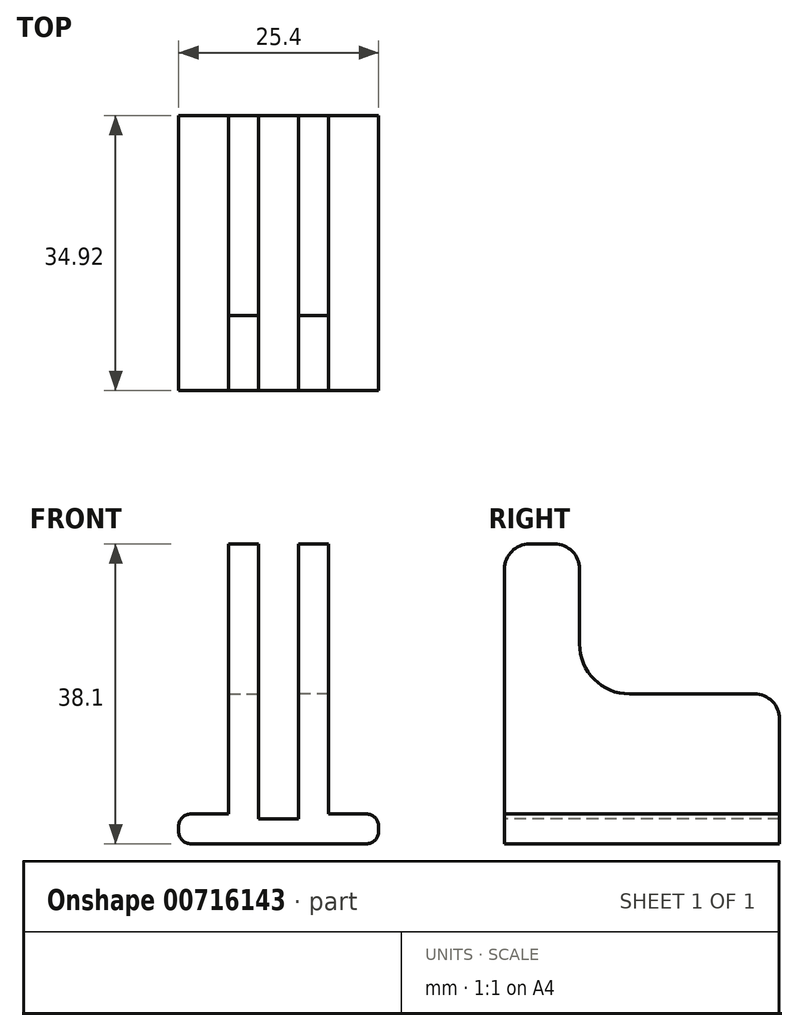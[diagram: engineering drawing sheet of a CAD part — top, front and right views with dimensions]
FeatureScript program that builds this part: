
annotation { "Feature Type Name" : "Feature", "Feature Type Description" : "" }
export const myFeature = defineFeature(function(context is Context, id is Id, definition is map)
    precondition{}
    {
        {
            var Q0;
            Q0=qCreatedBy(makeId("Right.planeOp"),FACE);
            var sketch = newSketch(context, id + "F0", { "sketchPlane" : qUnion([Q0])});
            skLineSegment(sketch, "E0", {"start": v(0, 0) * mm, "end": v(34.92, 0) * mm});
            skLineSegment(sketch, "E1", {"start": v(34.92, 0) * mm, "end": v(34.92, 15.88) * mm});
            skLineSegment(sketch, "E2", {"start": v(31.75, 19.05) * mm, "end": v(15.87, 19.05) * mm});
            skLineSegment(sketch, "E3", {"start": v(9.52, 25.4) * mm, "end": v(9.52, 34.93) * mm});
            skLineSegment(sketch, "E4", {"start": v(6.35, 38.1) * mm, "end": v(3.17, 38.1) * mm});
            skLineSegment(sketch, "E5", {"start": v(0, 34.93) * mm, "end": v(0, 0) * mm});
            skPoint(sketch, "E6.visualSharp", {"position": v(9.52, 19.05) * mm});
            skArc(sketch, "E6.filletArc", {"start": v(9.52, 25.4) * mm, "mid": v(11.38, 20.9) * mm, "end": v(15.87, 19.05) * mm});
            skPoint(sketch, "E7.visualSharp", {"position": v(34.92, 19.05) * mm});
            skArc(sketch, "E7.filletArc", {"start": v(34.92, 15.88) * mm, "mid": v(34, 18.12) * mm, "end": v(31.75, 19.05) * mm});
            skPoint(sketch, "E8.visualSharp", {"position": v(0, 38.1) * mm});
            skArc(sketch, "E8.filletArc", {"start": v(3.17, 38.1) * mm, "mid": v(0.93, 37.17) * mm, "end": v(0, 34.93) * mm});
            skPoint(sketch, "E9.visualSharp", {"position": v(9.52, 38.1) * mm});
            skArc(sketch, "E9.filletArc", {"start": v(9.52, 34.93) * mm, "mid": v(8.6, 37.17) * mm, "end": v(6.35, 38.1) * mm});
            skSolve(sketch);
        }
        {
            var Q0;
            Q0=qSketchRegion(id+"F0",true);
            extrude(context, id + "F1", {"entities" : qUnion([Q0]), "depth" : 3.8 * mm, "offsetDistance" : 25.4 * mm});
        }
        {
            var Q0;
            Q0=makeQuery(id+"F1.opExtrude","CAP_FACE",FACE,{"disambiguationData":[OSD([sQuery(id+"F0.wireOp",EDGE,"E0"),sQuery(id+"F0.wireOp",EDGE,"E1"),sQuery(id+"F0.wireOp",EDGE,"E2"),sQuery(id+"F0.wireOp",EDGE,"E3"),sQuery(id+"F0.wireOp",EDGE,"E4"),sQuery(id+"F0.wireOp",EDGE,"E5"),sQuery(id+"F0.wireOp",EDGE,"E6.filletArc"),sQuery(id+"F0.wireOp",EDGE,"E7.filletArc"),sQuery(id+"F0.wireOp",EDGE,"E8.filletArc"),sQuery(id+"F0.wireOp",EDGE,"E9.filletArc")])],"isStart":false});
            var sketch = newSketch(context, id + "F2", { "sketchPlane" : qUnion([Q0])});
            skLineSegment(sketch, "E10.bottom", {"start": v(0, 3.8) * mm, "end": v(34.92, 3.8) * mm});
            skLineSegment(sketch, "E10.top", {"start": v(0, 0) * mm, "end": v(34.92, 0) * mm});
            skLineSegment(sketch, "E10.left", {"start": v(0, 3.8) * mm, "end": v(0, 0) * mm});
            skLineSegment(sketch, "E10.right", {"start": v(34.92, 3.8) * mm, "end": v(34.92, 0) * mm});
            skPoint(sketch, "E10.middle", {"position": v(17.46, 1.9) * mm});
            skPoint(sketch, "E11.0", {"position": v(34.92, 0) * mm});
            skSolve(sketch);
        }
        {
            var Q0;
            Q0=qSketchRegion(id+"F2",true);
            extrude(context, id + "F3", {"entities" : qUnion([Q0]), "operationType" : NewBodyOperationType.ADD, "depth" : 6.35 * mm, "offsetDistance" : 25.4 * mm});
        }
        {
            var Q0;
            Q0=makeQuery(id+"F1.opExtrude","CAP_FACE",FACE,{"disambiguationData":[OSD([sQuery(id+"F0.wireOp",EDGE,"E0"),sQuery(id+"F0.wireOp",EDGE,"E1"),sQuery(id+"F0.wireOp",EDGE,"E2"),sQuery(id+"F0.wireOp",EDGE,"E3"),sQuery(id+"F0.wireOp",EDGE,"E4"),sQuery(id+"F0.wireOp",EDGE,"E5"),sQuery(id+"F0.wireOp",EDGE,"E6.filletArc"),sQuery(id+"F0.wireOp",EDGE,"E7.filletArc"),sQuery(id+"F0.wireOp",EDGE,"E8.filletArc"),sQuery(id+"F0.wireOp",EDGE,"E9.filletArc")])],"isStart":true});
            var sketch = newSketch(context, id + "F4", { "sketchPlane" : qUnion([Q0])});
            skLineSegment(sketch, "E12.bottom", {"start": v(-34.92, 3.17) * mm, "end": v(0, 3.17) * mm});
            skLineSegment(sketch, "E12.top", {"start": v(-34.92, 0) * mm, "end": v(0, 0) * mm});
            skLineSegment(sketch, "E12.left", {"start": v(-34.92, 3.17) * mm, "end": v(-34.92, 0) * mm});
            skLineSegment(sketch, "E12.right", {"start": v(0, 3.17) * mm, "end": v(0, 0) * mm});
            skPoint(sketch, "E12.middle", {"position": v(-17.46, 1.59) * mm});
            skSolve(sketch);
        }
        {
            var Q0;
            Q0=qSketchRegion(id+"F4",true);
            extrude(context, id + "F5", {"entities" : qUnion([Q0]), "operationType" : NewBodyOperationType.ADD, "depth" : 2.54 * mm, "offsetDistance" : 25.4 * mm});
        }
        {
            var Q0;
            Q0=makeQuery(id+"F3.opExtrude","CAP_EDGE",EDGE,{"disambiguationData":[OSD([sQuery(id+"F2.wireOp",EDGE,"E10.bottom")])],"isStart":true});
            var Q1;
            Q1=makeQuery(id+"F3.opExtrude","CAP_EDGE",EDGE,{"disambiguationData":[OSD([sQuery(id+"F2.wireOp",EDGE,"E10.bottom")])],"isStart":false});
            var Q2;
            Q2=makeQuery(id+"F5.opExtrude","CAP_EDGE",EDGE,{"disambiguationData":[OSD([sQuery(id+"F4.wireOp",EDGE,"E12.bottom")])],"isStart":true});
            var Q3;
            Q3=makeQuery(id+"F3.opExtrude","CAP_EDGE",EDGE,{"disambiguationData":[OSD([sQuery(id+"F2.wireOp",EDGE,"E10.top")])],"isStart":false});
            fillet(context, id + "F6", {"entities" : qUnion([Q0, Q1, Q2, Q3]), "tangentPropagation" : true, "radius" : 1.59 * mm, "defaultsChanged" : false, "vertexSettings" : [], "allowEdgeOverflow" : false});
        }
        {
            var Q0;
            Q0=makeQuery(id+"F1.opExtrude","SWEPT_BODY",BODY,{"disambiguationData":[OSD([sQuery(id+"F0.wireOp",EDGE,"E0"),sQuery(id+"F0.wireOp",EDGE,"E1"),sQuery(id+"F0.wireOp",EDGE,"E2"),sQuery(id+"F0.wireOp",EDGE,"E3"),sQuery(id+"F0.wireOp",EDGE,"E4"),sQuery(id+"F0.wireOp",EDGE,"E5"),sQuery(id+"F0.wireOp",EDGE,"E6.filletArc"),sQuery(id+"F0.wireOp",EDGE,"E7.filletArc"),sQuery(id+"F0.wireOp",EDGE,"E8.filletArc"),sQuery(id+"F0.wireOp",EDGE,"E9.filletArc")])]});
            var Q1;
            Q1=makeQuery(id+"F5.opExtrude","CAP_FACE",FACE,{"disambiguationData":[OSD([sQuery(id+"F4.wireOp",EDGE,"E12.bottom"),sQuery(id+"F4.wireOp",EDGE,"E12.top"),sQuery(id+"F4.wireOp",EDGE,"E12.left"),sQuery(id+"F4.wireOp",EDGE,"E12.right")])],"isStart":false});
            mirror(context, id + "F7", {"operationType" : NewBodyOperationType.ADD, "entities" : qUnion([Q0]), "mirrorPlane" : qUnion([Q1])});
        }
    });
